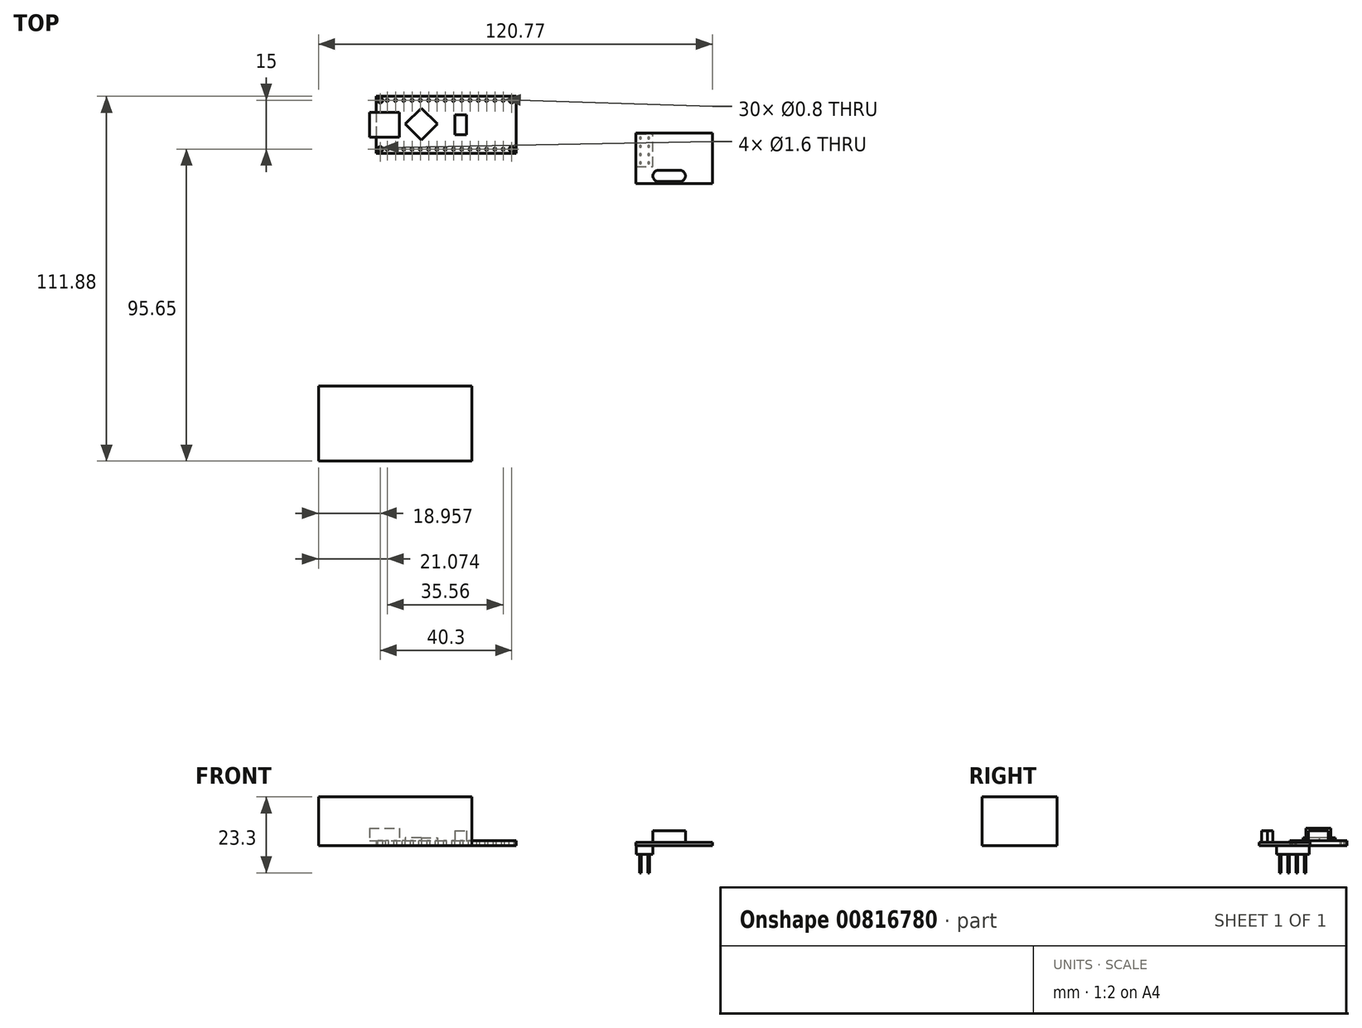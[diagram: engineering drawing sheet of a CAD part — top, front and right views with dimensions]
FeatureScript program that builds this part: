
annotation { "Feature Type Name" : "Feature", "Feature Type Description" : "" }
export const myFeature = defineFeature(function(context is Context, id is Id, definition is map)
    precondition{}
    {
        {
            var Q0;
            Q0=qCreatedBy(makeId("Top.planeOp"),FACE);
            var sketch = newSketch(context, id + "F0", { "sketchPlane" : qUnion([Q0])});
            skLineSegment(sketch, "E0.bottom", {"start": v(-53.63, 60.3) * mm, "end": v(-10.63, 60.3) * mm});
            skLineSegment(sketch, "E0.top", {"start": v(-53.63, 42.8) * mm, "end": v(-10.63, 42.8) * mm});
            skLineSegment(sketch, "E0.left", {"start": v(-53.63, 60.3) * mm, "end": v(-53.63, 42.8) * mm});
            skLineSegment(sketch, "E0.right", {"start": v(-10.63, 60.3) * mm, "end": v(-10.63, 42.8) * mm});
            skSolve(sketch);
        }
        {
            var Q0;
            Q0 = qSketchRegion(id + "F0", true);
            extrude(context, id + "F1", {"entities" : qUnion([Q0]), "depth" : 1.6 * mm, "offsetDistance" : 25 * mm});
        }
        {
            var Q0;
            Q0=makeQuery(id+"F1.opExtrude","CAP_FACE",FACE,{"disambiguationData":[OSD([sQuery(id+"F0.wireOp",EDGE,"E0.bottom"),sQuery(id+"F0.wireOp",EDGE,"E0.top"),sQuery(id+"F0.wireOp",EDGE,"E0.left"),sQuery(id+"F0.wireOp",EDGE,"E0.right")])],"isStart":false});
            var sketch = newSketch(context, id + "F2", { "sketchPlane" : qUnion([Q0])});
            skCircle(sketch, "E1", {"center": v(-52.31, 59.07) * mm, "radius": 0.8 * mm});
            skCircle(sketch, "E2", {"center": v(-12.01, 59.07) * mm, "radius": 0.8 * mm});
            skCircle(sketch, "E3", {"center": v(-52.31, 44.07) * mm, "radius": 0.8 * mm});
            skCircle(sketch, "E4", {"center": v(-12.01, 44.07) * mm, "radius": 0.8 * mm});
            skSolve(sketch);
        }
        {
            var Q0;
            Q0 = qSketchRegion(id + "F2", true);
            var Q1;
            Q1=makeQuery(id+"F1.opExtrude","CAP_FACE",FACE,{"disambiguationData":[OSD([sQuery(id+"F0.wireOp",EDGE,"E0.bottom"),sQuery(id+"F0.wireOp",EDGE,"E0.top"),sQuery(id+"F0.wireOp",EDGE,"E0.left"),sQuery(id+"F0.wireOp",EDGE,"E0.right")])],"isStart":true});
            extrude(context, id + "F3", {"entities" : qUnion([Q0]), "operationType" : NewBodyOperationType.REMOVE, "endBound" : BoundingType.UP_TO_SURFACE, "oppositeDirection" : true, "depth" : 25 * mm, "endBoundEntityFace" : qUnion([Q1]), "offsetDistance" : 25 * mm});
        }
        {
            var Q0;
            Q0=makeQuery(id+"F1.opExtrude","CAP_FACE",FACE,{"disambiguationData":[OSD([sQuery(id+"F0.wireOp",EDGE,"E0.bottom"),sQuery(id+"F0.wireOp",EDGE,"E0.top"),sQuery(id+"F0.wireOp",EDGE,"E0.left"),sQuery(id+"F0.wireOp",EDGE,"E0.right")])],"isStart":false});
            var sketch = newSketch(context, id + "F4", { "sketchPlane" : qUnion([Q0])});
            skCircle(sketch, "E5", {"center": v(-50.2, 59.07) * mm, "radius": 0.4 * mm});
            skCircle(sketch, "E6.1.0.0", {"center": v(-47.66, 59.07) * mm, "radius": 0.4 * mm});
            skCircle(sketch, "E6.2.0.0", {"center": v(-45.12, 59.07) * mm, "radius": 0.4 * mm});
            skLineSegment(sketch, "E6.direction1", {"start": v(-50.2, 59.07) * mm, "end": v(-47.66, 59.07) * mm, "construction": true});
            skCircle(sketch, "E7.0.3.0", {"center": v(-42.58, 59.07) * mm, "radius": 0.4 * mm});
            skCircle(sketch, "E7.0.4.0", {"center": v(-40.04, 59.07) * mm, "radius": 0.4 * mm});
            skCircle(sketch, "E7.0.5.0", {"center": v(-37.5, 59.07) * mm, "radius": 0.4 * mm});
            skCircle(sketch, "E7.0.6.0", {"center": v(-34.96, 59.07) * mm, "radius": 0.4 * mm});
            skCircle(sketch, "E7.0.7.0", {"center": v(-32.42, 59.07) * mm, "radius": 0.4 * mm});
            skCircle(sketch, "E7.0.8.0", {"center": v(-29.88, 59.07) * mm, "radius": 0.4 * mm});
            skCircle(sketch, "E7.0.9.0", {"center": v(-27.34, 59.07) * mm, "radius": 0.4 * mm});
            skCircle(sketch, "E7.0.10.0", {"center": v(-24.8, 59.07) * mm, "radius": 0.4 * mm});
            skCircle(sketch, "E7.0.11.0", {"center": v(-22.26, 59.07) * mm, "radius": 0.4 * mm});
            skCircle(sketch, "E7.0.12.0", {"center": v(-19.72, 59.07) * mm, "radius": 0.4 * mm});
            skCircle(sketch, "E7.0.13.0", {"center": v(-17.18, 59.07) * mm, "radius": 0.4 * mm});
            skCircle(sketch, "E7.0.14.0", {"center": v(-14.64, 59.07) * mm, "radius": 0.4 * mm});
            skCircle(sketch, "E8", {"center": v(-50.2, 44.07) * mm, "radius": 0.4 * mm});
            skCircle(sketch, "E9.1.0.0", {"center": v(-47.66, 44.07) * mm, "radius": 0.4 * mm});
            skCircle(sketch, "E9.2.0.0", {"center": v(-45.12, 44.07) * mm, "radius": 0.4 * mm});
            skLineSegment(sketch, "E9.direction1", {"start": v(-50.2, 44.07) * mm, "end": v(-47.66, 44.07) * mm, "construction": true});
            skCircle(sketch, "E10.0.3.0", {"center": v(-42.58, 44.07) * mm, "radius": 0.4 * mm});
            skCircle(sketch, "E10.0.4.0", {"center": v(-40.04, 44.07) * mm, "radius": 0.4 * mm});
            skCircle(sketch, "E10.0.5.0", {"center": v(-37.5, 44.07) * mm, "radius": 0.4 * mm});
            skCircle(sketch, "E10.0.6.0", {"center": v(-34.96, 44.07) * mm, "radius": 0.4 * mm});
            skCircle(sketch, "E10.0.7.0", {"center": v(-32.42, 44.07) * mm, "radius": 0.4 * mm});
            skCircle(sketch, "E10.0.8.0", {"center": v(-29.88, 44.07) * mm, "radius": 0.4 * mm});
            skCircle(sketch, "E10.0.9.0", {"center": v(-27.34, 44.07) * mm, "radius": 0.4 * mm});
            skCircle(sketch, "E10.0.10.0", {"center": v(-24.8, 44.07) * mm, "radius": 0.4 * mm});
            skCircle(sketch, "E10.0.11.0", {"center": v(-22.26, 44.07) * mm, "radius": 0.4 * mm});
            skCircle(sketch, "E10.0.12.0", {"center": v(-19.72, 44.07) * mm, "radius": 0.4 * mm});
            skCircle(sketch, "E10.0.13.0", {"center": v(-17.18, 44.07) * mm, "radius": 0.4 * mm});
            skCircle(sketch, "E10.0.14.0", {"center": v(-14.64, 44.07) * mm, "radius": 0.4 * mm});
            skCircle(sketch, "E11.0", {"center": v(-52.31, 59.07) * mm, "radius": 0.8 * mm, "construction": true});
            skCircle(sketch, "E12.0", {"center": v(-52.31, 44.07) * mm, "radius": 0.8 * mm, "construction": true});
            skSolve(sketch);
        }
        {
            var Q0;
            Q0 = qSketchRegion(id + "F4", true);
            var Q1;
            Q1=makeQuery(id+"F1.opExtrude","CAP_FACE",FACE,{"disambiguationData":[OSD([sQuery(id+"F0.wireOp",EDGE,"E0.bottom"),sQuery(id+"F0.wireOp",EDGE,"E0.top"),sQuery(id+"F0.wireOp",EDGE,"E0.left"),sQuery(id+"F0.wireOp",EDGE,"E0.right")])],"isStart":true});
            extrude(context, id + "F5", {"entities" : qUnion([Q0]), "operationType" : NewBodyOperationType.REMOVE, "endBound" : BoundingType.UP_TO_SURFACE, "oppositeDirection" : true, "depth" : 25 * mm, "endBoundEntityFace" : qUnion([Q1]), "offsetDistance" : 25 * mm});
        }
        {
            var Q0;
            Q0=makeQuery(id+"F1.opExtrude","CAP_FACE",FACE,{"disambiguationData":[OSD([sQuery(id+"F0.wireOp",EDGE,"E0.bottom"),sQuery(id+"F0.wireOp",EDGE,"E0.top"),sQuery(id+"F0.wireOp",EDGE,"E0.left"),sQuery(id+"F0.wireOp",EDGE,"E0.right")])],"isStart":false});
            var sketch = newSketch(context, id + "F6", { "sketchPlane" : qUnion([Q0])});
            skLineSegment(sketch, "E13.bottom", {"start": v(-55.63, 55.35) * mm, "end": v(-46.43, 55.35) * mm});
            skLineSegment(sketch, "E13.top", {"start": v(-55.63, 47.75) * mm, "end": v(-46.43, 47.75) * mm});
            skLineSegment(sketch, "E13.left", {"start": v(-55.63, 55.35) * mm, "end": v(-55.63, 47.75) * mm});
            skLineSegment(sketch, "E13.right", {"start": v(-46.43, 55.35) * mm, "end": v(-46.43, 47.75) * mm});
            skPoint(sketch, "E14", {"position": v(-53.63, 51.55) * mm});
            skPoint(sketch, "E15", {"position": v(-46.43, 51.55) * mm});
            skSolve(sketch);
        }
        {
            var Q0;
            Q0 = qSketchRegion(id + "F6", true);
            extrude(context, id + "F7", {"entities" : qUnion([Q0]), "operationType" : NewBodyOperationType.ADD, "depth" : 3.8 * mm, "offsetDistance" : 25 * mm});
        }
        {
            var Q0;
            Q0=makeQuery(id+"F1.opExtrude","CAP_FACE",FACE,{"disambiguationData":[OSD([sQuery(id+"F0.wireOp",EDGE,"E0.bottom"),sQuery(id+"F0.wireOp",EDGE,"E0.top"),sQuery(id+"F0.wireOp",EDGE,"E0.left"),sQuery(id+"F0.wireOp",EDGE,"E0.right")])],"isStart":false});
            var sketch = newSketch(context, id + "F8", { "sketchPlane" : qUnion([Q0])});
            skLineSegment(sketch, "E16.bottom", {"start": v(-39.78, 56.7) * mm, "end": v(-34.83, 51.75) * mm});
            skLineSegment(sketch, "E16.top", {"start": v(-44.73, 51.75) * mm, "end": v(-39.78, 46.8) * mm});
            skLineSegment(sketch, "E16.left", {"start": v(-39.78, 56.7) * mm, "end": v(-44.73, 51.75) * mm});
            skLineSegment(sketch, "E16.right", {"start": v(-34.83, 51.75) * mm, "end": v(-39.78, 46.8) * mm});
            skSolve(sketch);
        }
        {
            var Q0;
            Q0 = qSketchRegion(id + "F8", true);
            extrude(context, id + "F9", {"entities" : qUnion([Q0]), "operationType" : NewBodyOperationType.ADD, "depth" : 0.8 * mm, "offsetDistance" : 25 * mm});
        }
        {
            var Q0;
            Q0=makeQuery(id+"F1.opExtrude","CAP_FACE",FACE,{"disambiguationData":[OSD([sQuery(id+"F0.wireOp",EDGE,"E0.bottom"),sQuery(id+"F0.wireOp",EDGE,"E0.top"),sQuery(id+"F0.wireOp",EDGE,"E0.left"),sQuery(id+"F0.wireOp",EDGE,"E0.right")])],"isStart":false});
            var sketch = newSketch(context, id + "F10", { "sketchPlane" : qUnion([Q0])});
            skLineSegment(sketch, "E17.bottom", {"start": v(-29.42, 54.55) * mm, "end": v(-25.82, 54.55) * mm});
            skLineSegment(sketch, "E17.top", {"start": v(-29.42, 48.55) * mm, "end": v(-25.82, 48.55) * mm});
            skLineSegment(sketch, "E17.left", {"start": v(-29.42, 54.55) * mm, "end": v(-29.42, 48.55) * mm});
            skLineSegment(sketch, "E17.right", {"start": v(-25.82, 54.55) * mm, "end": v(-25.82, 48.55) * mm});
            skPoint(sketch, "E18", {"position": v(-10.63, 51.55) * mm});
            skPoint(sketch, "E19", {"position": v(-25.82, 51.55) * mm});
            skSolve(sketch);
        }
        {
            var Q0;
            Q0 = qSketchRegion(id + "F10", true);
            extrude(context, id + "F11", {"entities" : qUnion([Q0]), "operationType" : NewBodyOperationType.ADD, "depth" : 3 * mm, "offsetDistance" : 25 * mm});
        }
        {
            var Q0;
            Q0=qCreatedBy(makeId("Top.planeOp"),FACE);
            var sketch = newSketch(context, id + "F12", { "sketchPlane" : qUnion([Q0])});
            skLineSegment(sketch, "E20.bottom", {"start": v(26, 48.97) * mm, "end": v(49.5, 48.97) * mm});
            skLineSegment(sketch, "E20.top", {"start": v(26, 33.47) * mm, "end": v(49.5, 33.47) * mm});
            skLineSegment(sketch, "E20.left", {"start": v(26, 48.97) * mm, "end": v(26, 33.47) * mm});
            skLineSegment(sketch, "E20.right", {"start": v(49.5, 48.97) * mm, "end": v(49.5, 33.47) * mm});
            skSolve(sketch);
        }
        {
            var Q0;
            Q0 = qSketchRegion(id + "F12", true);
            extrude(context, id + "F13", {"entities" : qUnion([Q0]), "depth" : 1.1 * mm, "offsetDistance" : 25 * mm});
        }
        {
            var Q0;
            Q0=makeQuery(id+"F13.opExtrude","CAP_FACE",FACE,{"disambiguationData":[OSD([sQuery(id+"F12.wireOp",EDGE,"E20.bottom"),sQuery(id+"F12.wireOp",EDGE,"E20.top"),sQuery(id+"F12.wireOp",EDGE,"E20.left"),sQuery(id+"F12.wireOp",EDGE,"E20.right")])],"isStart":false});
            var sketch = newSketch(context, id + "F14", { "sketchPlane" : qUnion([Q0])});
            skLineSegment(sketch, "E21.bottom", {"start": v(31.28, 37.63) * mm, "end": v(41.28, 37.63) * mm});
            skLineSegment(sketch, "E21.top", {"start": v(31.28, 34.13) * mm, "end": v(41.28, 34.13) * mm});
            skLineSegment(sketch, "E21.left", {"start": v(31.28, 37.63) * mm, "end": v(31.28, 34.13) * mm});
            skLineSegment(sketch, "E21.right", {"start": v(41.28, 37.63) * mm, "end": v(41.28, 34.13) * mm});
            skSolve(sketch);
        }
        {
            var Q0;
            Q0 = qSketchRegion(id + "F14", true);
            extrude(context, id + "F15", {"entities" : qUnion([Q0]), "operationType" : NewBodyOperationType.ADD, "depth" : 3.5 * mm, "offsetDistance" : 25 * mm});
        }
        {
            var Q0;
            Q0=makeQuery(id+"F15.opExtrude","SWEPT_EDGE",EDGE,{"disambiguationData":[OSD([sQuery(id+"F14.wireOp",EDGE,"E21.top"),sQuery(id+"F14.wireOp",EDGE,"E21.left")])]});
            var Q1;
            Q1=makeQuery(id+"F15.opExtrude","SWEPT_EDGE",EDGE,{"disambiguationData":[OSD([sQuery(id+"F14.wireOp",EDGE,"E21.bottom"),sQuery(id+"F14.wireOp",EDGE,"E21.left")])]});
            var Q2;
            Q2=makeQuery(id+"F15.opExtrude","SWEPT_EDGE",EDGE,{"disambiguationData":[OSD([sQuery(id+"F14.wireOp",EDGE,"E21.bottom"),sQuery(id+"F14.wireOp",EDGE,"E21.right")])]});
            var Q3;
            Q3=makeQuery(id+"F15.opExtrude","SWEPT_EDGE",EDGE,{"disambiguationData":[OSD([sQuery(id+"F14.wireOp",EDGE,"E21.top"),sQuery(id+"F14.wireOp",EDGE,"E21.right")])]});
            fillet(context, id + "F16", {"entities" : qUnion([Q0, Q1, Q2, Q3]), "radius" : 1.8 * mm, "tangentPropagation" : true, "allowEdgeOverflow" : false});
        }
        {
            var Q0;
            Q0=makeQuery(id+"F13.opExtrude","CAP_FACE",FACE,{"disambiguationData":[OSD([sQuery(id+"F12.wireOp",EDGE,"E20.bottom"),sQuery(id+"F12.wireOp",EDGE,"E20.top"),sQuery(id+"F12.wireOp",EDGE,"E20.left"),sQuery(id+"F12.wireOp",EDGE,"E20.right")])],"isStart":true});
            var sketch = newSketch(context, id + "F17", { "sketchPlane" : qUnion([Q0])});
            skLineSegment(sketch, "E22.bottom", {"start": v(26.2, -38.75) * mm, "end": v(28.74, -38.75) * mm});
            skLineSegment(sketch, "E22.top", {"start": v(26.2, -41.15) * mm, "end": v(28.74, -41.15) * mm});
            skLineSegment(sketch, "E22.left", {"start": v(26.2, -38.75) * mm, "end": v(26.2, -41.15) * mm});
            skLineSegment(sketch, "E22.right", {"start": v(28.74, -38.75) * mm, "end": v(28.74, -41.15) * mm});
            skLineSegment(sketch, "E23.top", {"start": v(26.2, -43.69) * mm, "end": v(28.74, -43.69) * mm});
            skLineSegment(sketch, "E23.left", {"start": v(26.2, -41.15) * mm, "end": v(26.2, -43.69) * mm});
            skLineSegment(sketch, "E23.right", {"start": v(28.74, -41.15) * mm, "end": v(28.74, -43.69) * mm});
            skLineSegment(sketch, "E24.top", {"start": v(26.2, -46.23) * mm, "end": v(28.74, -46.23) * mm});
            skLineSegment(sketch, "E24.left", {"start": v(26.2, -43.69) * mm, "end": v(26.2, -46.23) * mm});
            skLineSegment(sketch, "E24.right", {"start": v(28.74, -43.69) * mm, "end": v(28.74, -46.23) * mm});
            skLineSegment(sketch, "E25.bottom", {"start": v(28.74, -38.75) * mm, "end": v(31.28, -38.75) * mm});
            skLineSegment(sketch, "E25.top", {"start": v(28.74, -41.29) * mm, "end": v(31.28, -41.29) * mm});
            skLineSegment(sketch, "E25.left", {"start": v(28.74, -38.75) * mm, "end": v(28.74, -41.29) * mm});
            skLineSegment(sketch, "E25.right", {"start": v(31.28, -38.75) * mm, "end": v(31.28, -41.29) * mm});
            skLineSegment(sketch, "E26.bottom", {"start": v(28.74, -46.23) * mm, "end": v(31.28, -46.23) * mm});
            skLineSegment(sketch, "E26.top", {"start": v(28.74, -48.77) * mm, "end": v(31.28, -48.77) * mm});
            skLineSegment(sketch, "E26.left", {"start": v(28.74, -46.23) * mm, "end": v(28.74, -48.77) * mm});
            skLineSegment(sketch, "E26.right", {"start": v(31.28, -46.23) * mm, "end": v(31.28, -48.77) * mm});
            skLineSegment(sketch, "E27.top", {"start": v(26.2, -48.77) * mm, "end": v(28.74, -48.77) * mm});
            skLineSegment(sketch, "E27.left", {"start": v(26.2, -46.23) * mm, "end": v(26.2, -48.77) * mm});
            skLineSegment(sketch, "E28.bottom", {"start": v(28.74, -41.15) * mm, "end": v(31.28, -41.15) * mm});
            skLineSegment(sketch, "E28.top", {"start": v(28.74, -43.69) * mm, "end": v(31.28, -43.69) * mm});
            skLineSegment(sketch, "E28.right", {"start": v(31.28, -41.15) * mm, "end": v(31.28, -43.69) * mm});
            skLineSegment(sketch, "E29.right", {"start": v(31.28, -43.69) * mm, "end": v(31.28, -46.23) * mm});
            skSolve(sketch);
        }
        {
            var Q0;
            Q0 = qSketchRegion(id + "F17", true);
            extrude(context, id + "F18", {"entities" : qUnion([Q0]), "operationType" : NewBodyOperationType.ADD, "depth" : 2.6 * mm, "offsetDistance" : 25 * mm});
        }
        {
            var Q0;
            Q0=makeQuery(id+"F18.opExtrude","CAP_FACE",FACE,{"disambiguationData":[OSD([sQuery(id+"F17.wireOp",EDGE,"E22.bottom"),sQuery(id+"F17.wireOp",EDGE,"E22.left"),sQuery(id+"F17.wireOp",EDGE,"E23.left"),sQuery(id+"F17.wireOp",EDGE,"E24.left"),sQuery(id+"F17.wireOp",EDGE,"E25.bottom"),sQuery(id+"F17.wireOp",EDGE,"E25.right"),sQuery(id+"F17.wireOp",EDGE,"E26.top"),sQuery(id+"F17.wireOp",EDGE,"E26.right"),sQuery(id+"F17.wireOp",EDGE,"E27.top"),sQuery(id+"F17.wireOp",EDGE,"E27.left"),sQuery(id+"F17.wireOp",EDGE,"E28.right"),sQuery(id+"F17.wireOp",EDGE,"E29.right")])],"isStart":false});
            var sketch = newSketch(context, id + "F19", { "sketchPlane" : qUnion([Q0])});
            skCircle(sketch, "E30", {"center": v(27.47, -47.5) * mm, "radius": 0.3 * mm});
            skCircle(sketch, "E31.0.1.0", {"center": v(27.47, -44.96) * mm, "radius": 0.3 * mm});
            skCircle(sketch, "E31.0.2.0", {"center": v(27.47, -42.42) * mm, "radius": 0.3 * mm});
            skCircle(sketch, "E31.0.3.0", {"center": v(27.47, -39.88) * mm, "radius": 0.3 * mm});
            skCircle(sketch, "E31.1.0.0", {"center": v(30.01, -47.5) * mm, "radius": 0.3 * mm});
            skCircle(sketch, "E31.1.1.0", {"center": v(30.01, -44.96) * mm, "radius": 0.3 * mm});
            skCircle(sketch, "E31.1.2.0", {"center": v(30.01, -42.42) * mm, "radius": 0.3 * mm});
            skCircle(sketch, "E31.1.3.0", {"center": v(30.01, -39.88) * mm, "radius": 0.3 * mm});
            skLineSegment(sketch, "E31.direction1", {"start": v(27.47, -47.5) * mm, "end": v(30.01, -47.5) * mm, "construction": true});
            skLineSegment(sketch, "E31.direction2", {"start": v(27.47, -47.5) * mm, "end": v(27.47, -44.96) * mm, "construction": true});
            skSolve(sketch);
        }
        {
            var Q0;
            Q0 = qSketchRegion(id + "F19", true);
            extrude(context, id + "F20", {"entities" : qUnion([Q0]), "operationType" : NewBodyOperationType.ADD, "depth" : 5.7 * mm, "offsetDistance" : 25 * mm});
        }
        {
            var Q0;
            Q0=qCreatedBy(makeId("Top.planeOp"),FACE);
            var sketch = newSketch(context, id + "F21", { "sketchPlane" : qUnion([Q0])});
            skLineSegment(sketch, "E32.bottom", {"start": v(-71.27, -28.58) * mm, "end": v(-24.27, -28.58) * mm});
            skLineSegment(sketch, "E32.top", {"start": v(-71.27, -51.58) * mm, "end": v(-24.27, -51.58) * mm});
            skLineSegment(sketch, "E32.left", {"start": v(-71.27, -28.58) * mm, "end": v(-71.27, -51.58) * mm});
            skLineSegment(sketch, "E32.right", {"start": v(-24.27, -28.58) * mm, "end": v(-24.27, -51.58) * mm});
            skSolve(sketch);
        }
        {
            var Q0;
            Q0 = qSketchRegion(id + "F21", true);
            extrude(context, id + "F22", {"entities" : qUnion([Q0]), "depth" : 15 * mm, "offsetDistance" : 25 * mm});
        }
    });
